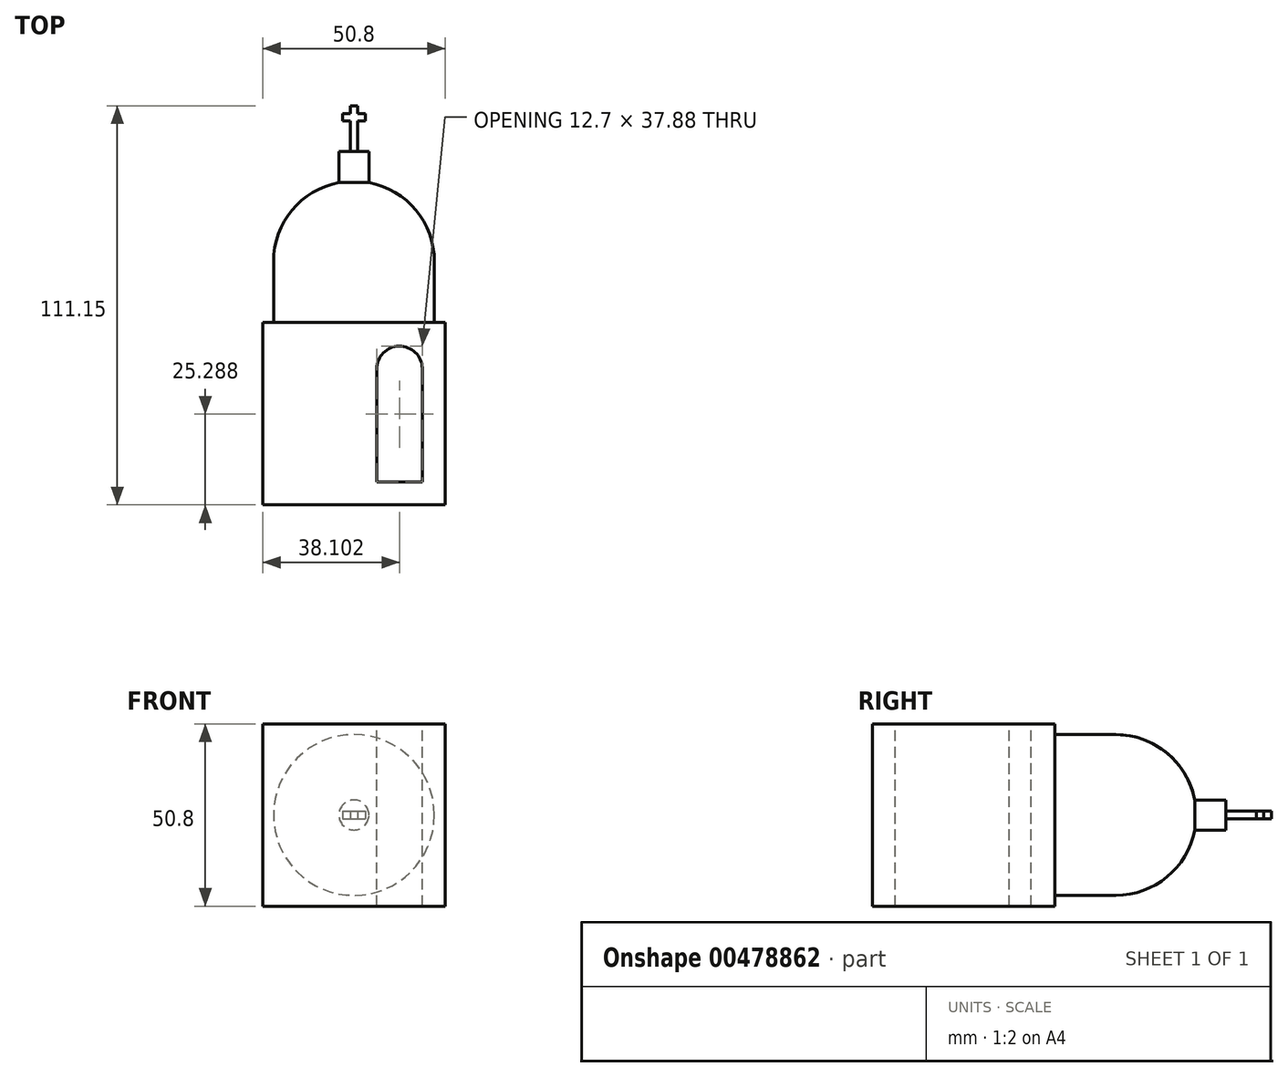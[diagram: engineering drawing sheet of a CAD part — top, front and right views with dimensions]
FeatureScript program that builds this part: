
annotation { "Feature Type Name" : "Feature", "Feature Type Description" : "" }
export const myFeature = defineFeature(function(context is Context, id is Id, definition is map)
    precondition{}
    {
        {
            var Q0;
            Q0=qCreatedBy(makeId("Top.planeOp"),FACE);
            var sketch = newSketch(context, id + "F0", { "sketchPlane" : qUnion([Q0])});
            skLineSegment(sketch, "E0.bottom", {"start": v(25.4, 25.4) * mm, "end": v(-25.4, 25.4) * mm});
            skLineSegment(sketch, "E0.top", {"start": v(25.4, -25.4) * mm, "end": v(-25.4, -25.4) * mm});
            skLineSegment(sketch, "E0.left", {"start": v(25.4, 25.4) * mm, "end": v(25.4, -25.4) * mm});
            skLineSegment(sketch, "E0.right", {"start": v(-25.4, 25.4) * mm, "end": v(-25.4, -25.4) * mm});
            skPoint(sketch, "E0.middle", {"position": v(0, 0) * mm});
            skLineSegment(sketch, "E1", {"start": v(-22.4, 25.4) * mm, "end": v(-22.4, 42.42) * mm});
            skLineSegment(sketch, "E2", {"start": v(-22.4, 42.42) * mm, "end": v(0, 42.42) * mm});
            skLineSegment(sketch, "E3", {"start": v(0, 42.42) * mm, "end": v(0, 25.4) * mm});
            skLineSegment(sketch, "E4", {"start": v(0, 60.09) * mm, "end": v(0, 42.42) * mm});
            skLineSegment(sketch, "E5", {"start": v(0, 60.09) * mm, "end": v(0, 69.62) * mm});
            skLineSegment(sketch, "E6", {"start": v(-1.05, 73.03) * mm, "end": v(-1.05, 81.53) * mm});
            skLineSegment(sketch, "E7", {"start": v(-1.05, 81.53) * mm, "end": v(-3.16, 81.53) * mm});
            skLineSegment(sketch, "E8", {"start": v(-3.16, 81.53) * mm, "end": v(-3.16, 83.64) * mm});
            skLineSegment(sketch, "E9", {"start": v(-3.16, 83.64) * mm, "end": v(-1.05, 83.64) * mm});
            skLineSegment(sketch, "E10", {"start": v(-1.05, 83.64) * mm, "end": v(-1.05, 85.75) * mm});
            skLineSegment(sketch, "E11", {"start": v(-1.05, 85.75) * mm, "end": v(0, 85.75) * mm});
            skLineSegment(sketch, "E12", {"start": v(-19.05, -19.05) * mm, "end": v(-19.05, 12.7) * mm});
            skLineSegment(sketch, "E13", {"start": v(0, 25.4) * mm, "end": v(0, -25.4) * mm});
            skLineSegment(sketch, "E14", {"start": v(-19.05, -19.05) * mm, "end": v(-6.35, -19.05) * mm});
            skLineSegment(sketch, "E15", {"start": v(-6.35, -19.05) * mm, "end": v(-6.35, 12.48) * mm});
            skLineSegment(sketch, "E16.MirrorCS", {"start": v(6.35, -19.05) * mm, "end": v(6.35, 12.48) * mm});
            skLineSegment(sketch, "E17.MirrorCS", {"start": v(19.05, -19.05) * mm, "end": v(6.35, -19.05) * mm});
            skLineSegment(sketch, "E18.MirrorCS", {"start": v(19.05, -19.05) * mm, "end": v(19.05, 12.7) * mm});
            skArc(sketch, "E19", {"start": v(-6.35, 12.48) * mm, "mid": v(-12.6, 18.83) * mm, "end": v(-19.05, 12.7) * mm});
            skArc(sketch, "E20.MirrorCS", {"start": v(6.35, 12.48) * mm, "mid": v(12.6, 18.83) * mm, "end": v(19.05, 12.7) * mm});
            skPoint(sketch, "E21.MirrorCS.end.orphan", {"position": v(6.35, 12.48) * mm});
            skPoint(sketch, "E21.MirrorCS.start.orphan", {"position": v(19.05, 12.7) * mm});
            skArc(sketch, "E22", {"start": v(-22.4, 42.42) * mm, "mid": v(-15.84, 58.25) * mm, "end": v(0, 64.81) * mm});
            skLineSegment(sketch, "E23", {"start": v(-4.2, 73.03) * mm, "end": v(-4.2, 64.42) * mm});
            skLineSegment(sketch, "E24", {"start": v(-4.2, 73.03) * mm, "end": v(0, 73.03) * mm});
            skLineSegment(sketch, "E25", {"start": v(0, 69.62) * mm, "end": v(0, 85.75) * mm});
            skLineSegment(sketch, "E26.MirrorCS", {"start": v(1.05, 73.03) * mm, "end": v(1.05, 81.53) * mm});
            skLineSegment(sketch, "E27.MirrorCS", {"start": v(1.05, 81.53) * mm, "end": v(3.16, 81.53) * mm});
            skLineSegment(sketch, "E28.MirrorCS", {"start": v(3.16, 81.53) * mm, "end": v(3.16, 83.64) * mm});
            skLineSegment(sketch, "E29.MirrorCS", {"start": v(3.16, 83.64) * mm, "end": v(1.05, 83.64) * mm});
            skLineSegment(sketch, "E30.MirrorCS", {"start": v(1.05, 85.75) * mm, "end": v(0, 85.75) * mm});
            skLineSegment(sketch, "E31.MirrorCS", {"start": v(1.05, 83.64) * mm, "end": v(1.05, 85.75) * mm});
            skLineSegment(sketch, "E32.MirrorCS", {"start": v(1.05, 73.03) * mm, "end": v(0, 73.03) * mm});
            skSolve(sketch);
        }
        {
            var Q0;
            Q0=makeQuery(id+"F0.imprint","IMPRINT",FACE,{"disambiguationData":[TD([[makeQuery(id+"F0.imprint","IMPRINT",EDGE,{"derivedFrom":sQuery(id+"F0.wireOp",EDGE,"E0.bottom")}),1.0]])]});
            var Q1;
            {var subQ1=sQuery(id+"F0.wireOp",EDGE,"E0.left");Q1=makeQuery(id+"F0.imprint","IMPRINT",FACE,{"disambiguationData":[TD([[makeQuery(id+"F0.imprint","IMPRINT",EDGE,{"derivedFrom":subQ1}),-1.0]])]});}
            var Q2;
            Q2=makeQuery(id+"F0.imprint","IMPRINT",FACE,{"disambiguationData":[TD([[makeQuery(id+"F0.imprint","IMPRINT",EDGE,{"derivedFrom":sQuery(id+"F0.wireOp",EDGE,"E12")}),-1.0]])]});
            var Q3;
            Q3=makeQuery(id+"F0.imprint","IMPRINT",FACE,{"disambiguationData":[TD([[makeQuery(id+"F0.imprint","IMPRINT",EDGE,{"derivedFrom":sQuery(id+"F0.wireOp",EDGE,"E16.MirrorCS")}),-1.0]])]});
            extrude(context, id + "F1", {"entities" : qUnion([Q0, Q1, Q2, Q3]), "depth" : 50.8 * mm, "symmetric" : true});
        }
        {
            var Q0;
            {var subQ0=sQuery(id+"F0.wireOp",EDGE,"E1");Q0=makeQuery(id+"F0.imprint","IMPRINT",FACE,{"disambiguationData":[TD([[makeQuery(id+"F0.imprint","IMPRINT",EDGE,{"derivedFrom":subQ0}),-1.0]])]});}
            var Q1;
            {var subQ0=sQuery(id+"F0.wireOp",EDGE,"E2");Q1=makeQuery(id+"F0.imprint","IMPRINT",FACE,{"disambiguationData":[TD([[makeQuery(id+"F0.imprint","IMPRINT",EDGE,{"derivedFrom":subQ0}),1.0]])]});}
            var Q2;
            {var subQ2=sQuery(id+"F0.wireOp",EDGE,"o4DFvwhS-giHV-mI0n-EIcg-HC2yWQCYLwaE");Q2=makeQuery(id+"F0.imprint","IMPRINT",FACE,{"disambiguationData":[TD([[makeQuery(id+"F0.imprint","IMPRINT",EDGE,{"derivedFrom":subQ2}),-1.0]])]});}
            var Q3;
            {var subQ2=sQuery(id+"F0.wireOp",EDGE,"E23");Q3=makeQuery(id+"F0.imprint","IMPRINT",FACE,{"disambiguationData":[TD([[makeQuery(id+"F0.imprint","IMPRINT",EDGE,{"derivedFrom":subQ2}),1.0]])]});}
            var Q4;
            Q4=sQuery(id+"F0.wireOp",EDGE,"E4");
            revolve(context, id + "F2", {"operationType" : NewBodyOperationType.ADD, "entities" : qUnion([Q0, Q1, Q2, Q3]), "axis" : qUnion([Q4]), "revolveType" : RevolveType.FULL});
        }
        {
            var Q0;
            {var subQ0=sQuery(id+"F0.wireOp",EDGE,"E6");Q0=makeQuery(id+"F0.imprint","IMPRINT",FACE,{"disambiguationData":[TD([[makeQuery(id+"F0.imprint","IMPRINT",EDGE,{"derivedFrom":subQ0}),-1.0]])]});}
            var Q1;
            Q1=makeQuery(id+"F0.imprint","IMPRINT",FACE,{"disambiguationData":[TD([[makeQuery(id+"F0.imprint","IMPRINT",EDGE,{"derivedFrom":sQuery(id+"F0.wireOp",EDGE,"Efs2OtlG-23bB-Sr3K-T8Hr-gcVjpuxsdwrl")}),1.0]])]});
            var Q2;
            {var subQ0=sQuery(id+"F0.wireOp",EDGE,"e169aa30-478e-474d-8dbb-06b81f504d840.MirrorCS");Q2=makeQuery(id+"F0.imprint","IMPRINT",FACE,{"disambiguationData":[TD([[makeQuery(id+"F0.imprint","IMPRINT",EDGE,{"derivedFrom":subQ0}),1.0]])]});}
            var Q3;
            Q3=makeQuery(id+"F0.imprint","IMPRINT",FACE,{"disambiguationData":[TD([[makeQuery(id+"F0.imprint","IMPRINT",EDGE,{"derivedFrom":sQuery(id+"F0.wireOp",EDGE,"E26.MirrorCS")}),1.0]])]});
            extrude(context, id + "F3", {"entities" : qUnion([Q0, Q1, Q2, Q3]), "operationType" : NewBodyOperationType.ADD, "depth" : 2.1 * mm, "symmetric" : true});
        }
        {
            var Q0;
            Q0=makeQuery(id+"F0.imprint","IMPRINT",FACE,{"disambiguationData":[TD([[makeQuery(id+"F0.imprint","IMPRINT",EDGE,{"derivedFrom":sQuery(id+"F0.wireOp",EDGE,"E16.MirrorCS")}),-1.0]])]});
            extrude(context, id + "F4", {"entities" : qUnion([Q0]), "operationType" : NewBodyOperationType.REMOVE, "oppositeDirection" : true, "depth" : 50.8 * mm, "symmetric" : true});
        }
    });
